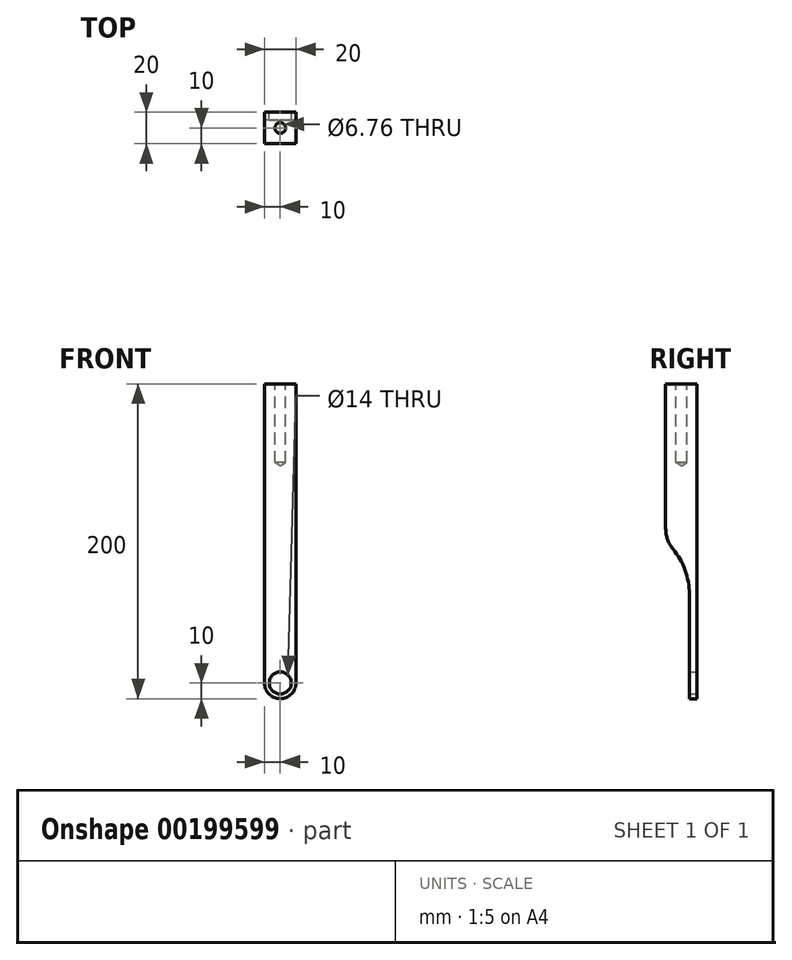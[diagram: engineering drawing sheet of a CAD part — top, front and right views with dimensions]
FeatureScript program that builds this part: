
annotation { "Feature Type Name" : "Feature", "Feature Type Description" : "" }
export const myFeature = defineFeature(function(context is Context, id is Id, definition is map)
    precondition{}
    {
        {
            var Q0;
            Q0=qCreatedBy(makeId("Front.planeOp"),FACE);
            var sketch = newSketch(context, id + "F0", { "sketchPlane" : qUnion([Q0])});
            skLineSegment(sketch, "E0.bottom", {"start": v(0, 0) * mm, "end": v(20, 0) * mm});
            skLineSegment(sketch, "E0.top", {"start": v(0, 200) * mm, "end": v(20, 200) * mm});
            skLineSegment(sketch, "E0.left", {"start": v(0, 0) * mm, "end": v(0, 200) * mm});
            skLineSegment(sketch, "E0.right", {"start": v(20, 0) * mm, "end": v(20, 200) * mm});
            skSolve(sketch);
        }
        {
            var Q0;
            Q0 = qSketchRegion(id + "F0", true);
            extrude(context, id + "F1", {"entities" : qUnion([Q0]), "depth" : 20 * mm});
        }
        {
            var Q0;
            Q0=makeQuery(id+"F1.opExtrude","SWEPT_FACE",FACE,{"disambiguationData":[OSD([sQuery(id+"F0.wireOp",EDGE,"E0.right")])]});
            var sketch = newSketch(context, id + "F2", { "sketchPlane" : qUnion([Q0])});
            skLineSegment(sketch, "E1.bottom", {"start": v(-20, 0) * mm, "end": v(-5, 0) * mm});
            skLineSegment(sketch, "E1.top", {"start": v(-20, 100) * mm, "end": v(-5, 100) * mm});
            skLineSegment(sketch, "E1.left", {"start": v(-20, 0) * mm, "end": v(-20, 100) * mm});
            skLineSegment(sketch, "E1.right", {"start": v(-5, 0) * mm, "end": v(-5, 100) * mm});
            skSolve(sketch);
        }
        {
            var Q0;
            Q0=makeQuery(id+"F2.imprint","IMPRINT",FACE,{"disambiguationData":[TD([[makeQuery(id+"F2.imprint","IMPRINT",EDGE,{"derivedFrom":sQuery(id+"F2.wireOp",EDGE,"E1.bottom")}),1.0]])]});
            extrude(context, id + "F3", {"entities" : qUnion([Q0]), "operationType" : NewBodyOperationType.REMOVE, "oppositeDirection" : true, "depth" : 20 * mm});
        }
        {
            var Q0;
            Q0=makeQuery(id+"F1.opExtrude","CAP_FACE",FACE,{"disambiguationData":[OSD([sQuery(id+"F0.wireOp",EDGE,"E0.bottom"),sQuery(id+"F0.wireOp",EDGE,"E0.top"),sQuery(id+"F0.wireOp",EDGE,"E0.left"),sQuery(id+"F0.wireOp",EDGE,"E0.right")])],"isStart":true});
            var sketch = newSketch(context, id + "F4", { "sketchPlane" : qUnion([Q0])});
            skCircle(sketch, "E2", {"center": v(-10, 10) * mm, "radius": 10 * mm});
            skPoint(sketch, "E2.centerSnap0", {"position": v(-10, 0) * mm});
            skSolve(sketch);
        }
        {
            var Q0;
            {var subQ0=sQuery(id+"F4.wireOp",EDGE,"E2");var subQ1=makeQuery(id+"F1.opExtrude","CAP_EDGE",EDGE,{"disambiguationData":[OSD([sQuery(id+"F0.wireOp",EDGE,"E0.left")])],"isStart":true});var subQ2=makeQuery(id+"F4.imprint","INTERSECT",VERTEX,{"derivedFrom":[subQ1,subQ0]});Q0=makeQuery(id+"F4.imprint","IMPRINT",FACE,{"disambiguationData":[TD([[makeQuery(id+"F4.imprint","IMPRINT",EDGE,{"disambiguationData":[TD([[subQ2,1.0]])],"derivedFrom":subQ0}),-1.0]])]});}
            var Q1;
            {var subQ0=sQuery(id+"F4.wireOp",EDGE,"E2");var subQ1=makeQuery(id+"F1.opExtrude","CAP_EDGE",EDGE,{"disambiguationData":[OSD([sQuery(id+"F0.wireOp",EDGE,"E0.right")])],"isStart":true});var subQ2=makeQuery(id+"F4.imprint","INTERSECT",VERTEX,{"derivedFrom":[subQ1,subQ0]});Q1=makeQuery(id+"F4.imprint","IMPRINT",FACE,{"disambiguationData":[TD([[makeQuery(id+"F4.imprint","IMPRINT",EDGE,{"disambiguationData":[TD([[subQ2,-1.0]])],"derivedFrom":subQ0}),-1.0]])]});}
            var Q2;
            Q2=makeQuery(id+"F1.opExtrude","SWEPT_EDGE",EDGE,{"disambiguationData":[OSD([sQuery(id+"F0.wireOp",EDGE,"E0.bottom"),sQuery(id+"F0.wireOp",EDGE,"E0.left")])]});
            sweep(context, id + "F5", {"operationType" : NewBodyOperationType.REMOVE, "profiles" : qUnion([Q0, Q1]), "path" : qUnion([Q2])});
        }
        {
            var Q0;
            Q0=makeQuery(id+"F1.opExtrude","CAP_FACE",FACE,{"disambiguationData":[OSD([sQuery(id+"F0.wireOp",EDGE,"E0.bottom"),sQuery(id+"F0.wireOp",EDGE,"E0.top"),sQuery(id+"F0.wireOp",EDGE,"E0.left"),sQuery(id+"F0.wireOp",EDGE,"E0.right")])],"isStart":true});
            var sketch = newSketch(context, id + "F6", { "sketchPlane" : qUnion([Q0])});
            skCircle(sketch, "E3", {"center": v(-10, 10) * mm, "radius": 7 * mm});
            skSolve(sketch);
        }
        {
            var Q0;
            Q0 = qSketchRegion(id + "F6", true);
            extrude(context, id + "F7", {"entities" : qUnion([Q0]), "operationType" : NewBodyOperationType.REMOVE, "endBound" : BoundingType.THROUGH_ALL, "oppositeDirection" : true, "depth" : 25 * mm});
        }
        {
            var Q0;
            Q0=makeQuery(id+"F3.boolean.opBoolean","COPY",EDGE,{"derivedFrom":makeQuery(id+"F3.opExtrude","SWEPT_EDGE",EDGE,{"disambiguationData":[OSD([sQuery(id+"F2.wireOp",EDGE,"E1.top"),sQuery(id+"F2.wireOp",EDGE,"E1.right")])]})});
            fillet(context, id + "F8", {"entities" : qUnion([Q0]), "radius" : 45 * mm, "tangentPropagation" : true, "allowEdgeOverflow" : false});
        }
        {
            var Q0;
            Q0=makeQuery(id+"F8.opFillet","BLEND_EDGE",EDGE,{"blendedFrom":[makeQuery(id+"F3.boolean.opBoolean","COPY",EDGE,{"derivedFrom":makeQuery(id+"F3.opExtrude","SWEPT_EDGE",EDGE,{"disambiguationData":[OSD([sQuery(id+"F2.wireOp",EDGE,"E1.top"),sQuery(id+"F2.wireOp",EDGE,"E1.right")])]})}),makeQuery(id+"F1.opExtrude","CAP_FACE",FACE,{"disambiguationData":[OSD([sQuery(id+"F0.wireOp",EDGE,"E0.bottom"),sQuery(id+"F0.wireOp",EDGE,"E0.top"),sQuery(id+"F0.wireOp",EDGE,"E0.left"),sQuery(id+"F0.wireOp",EDGE,"E0.right")])],"isStart":false})],"blendedInto":[makeQuery(id+"F1.opExtrude","CAP_FACE",FACE,{"disambiguationData":[OSD([sQuery(id+"F0.wireOp",EDGE,"E0.bottom"),sQuery(id+"F0.wireOp",EDGE,"E0.top"),sQuery(id+"F0.wireOp",EDGE,"E0.left"),sQuery(id+"F0.wireOp",EDGE,"E0.right")])],"isStart":false})]});
            fillet(context, id + "F9", {"entities" : qUnion([Q0]), "radius" : 20 * mm, "tangentPropagation" : true, "allowEdgeOverflow" : false});
        }
        {
            var Q0;
            Q0=makeQuery(id+"F1.opExtrude","SWEPT_FACE",FACE,{"disambiguationData":[OSD([sQuery(id+"F0.wireOp",EDGE,"E0.top")])]});
            var sketch = newSketch(context, id + "F10", { "sketchPlane" : qUnion([Q0])});
            skPoint(sketch, "E4", {"position": v(10, -10) * mm});
            skSolve(sketch);
        }
        {
            var Q0;
            Q0=sQuery(id+"F10.wireOp",VERTEX,"E4");
            var Q1;
            Q1=makeQuery(id+"F1.opExtrude","SWEPT_BODY",BODY,{"disambiguationData":[OSD([sQuery(id+"F0.wireOp",EDGE,"E0.bottom"),sQuery(id+"F0.wireOp",EDGE,"E0.top"),sQuery(id+"F0.wireOp",EDGE,"E0.left"),sQuery(id+"F0.wireOp",EDGE,"E0.right")])]});
            hole(context, id + "F11", {"style" : HoleStyle.SIMPLE, "endStyle" : HoleEndStyle.BLIND, "standardTappedOrClearance" : lookupTablePath({ "standard" : "ANSI", "fit" : "Normal (ASME)", "size" : "1/4", "type" : "Clearance" }), "standardBlindInLast" : lookupTablePath({ "fit" : "Free", "standard" : "ANSI", "size" : "1/4", "type" : "Clearance" }), "holeDiameter" : 6.76 * mm, "holeDepth" : 50 * mm, "locations" : qUnion([Q0]), "scope" : qUnion([Q1])});
        }
    });
